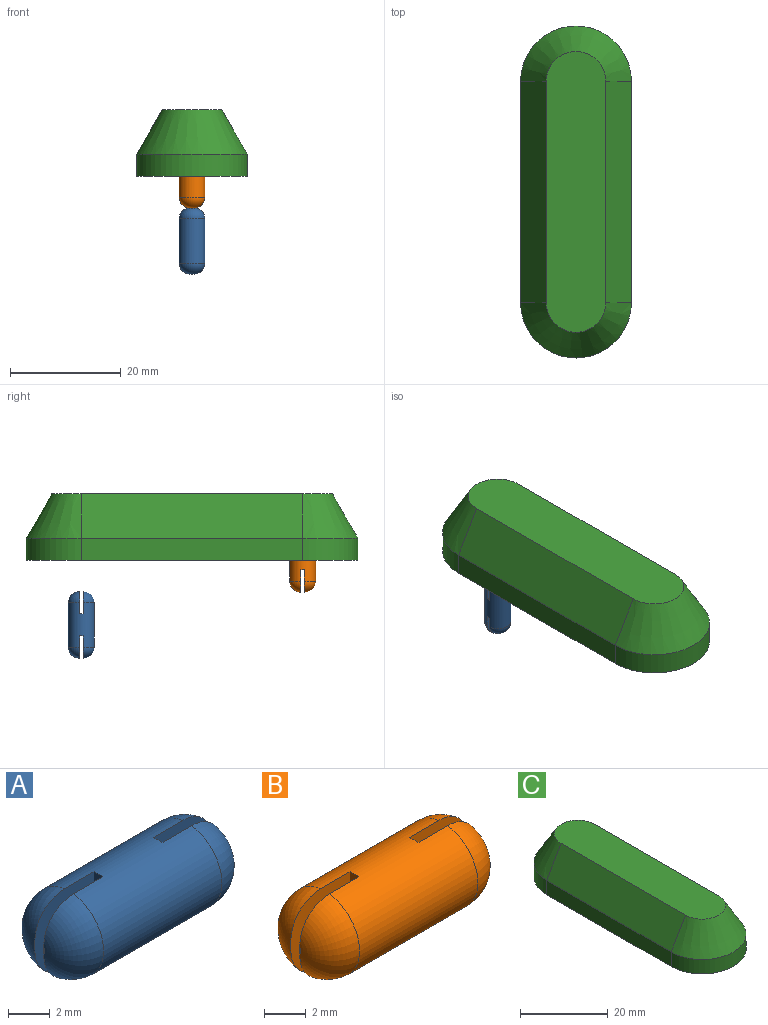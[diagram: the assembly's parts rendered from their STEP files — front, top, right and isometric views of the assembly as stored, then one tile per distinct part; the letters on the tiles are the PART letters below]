
ASSEMBLY  parts=3 mates=2
PART A: 15 faces, bbox 12x4.7x4.7 mm
  f0: plane 0.36x0.05mm, normal (1,0,0), area 0mm2, adj f1,f13
  f1: torus R=0.35mm, axis (1,0,0), area 14.1mm2, adj f0,f4,f13
  f2: plane 0.36x0.05mm, normal (-1,0,0), area 0mm2, adj f7,f10
  f3: torus R=0.35mm, axis (1,0,0), area 14.1mm2, adj f4,f6,f11
  f4: cylinder r=2.35mm len=8mm, axis (-1,0,0), area 113.3mm2, adj f1,f3,f7,f8,f9,f10,f11,f12
  f5: plane 0.36x0.05mm, normal (1,0,0), area 0mm2, adj f8,f14
  f6: plane 0.36x0.05mm, normal (-1,0,0), area 0mm2, adj f3,f11
  f7: torus R=0.35mm, axis (1,0,0), area 14.1mm2, adj f2,f4,f10
  f8: torus R=0.35mm, axis (1,0,0), area 14.1mm2, adj f4,f5,f14
  f9: plane 4.7x0.6mm, normal (-1,0,0), area 2.8mm2, adj f4,f10,f11
  f10: plane 4.66x4mm, normal (0,1,0), area 16.9mm2, adj f2,f4,f7,f9
  f11: plane 4.66x4mm, normal (0,-1,0), area 16.9mm2, adj f3,f4,f6,f9
  f12: plane 4.7x0.6mm, normal (1,0,0), area 2.8mm2, adj f4,f13,f14
  f13: plane 4.66x4mm, normal (0,1,0), area 16.9mm2, adj f0,f1,f4,f12
  f14: plane 4.66x4mm, normal (0,-1,0), area 16.9mm2, adj f4,f5,f8,f12
PART B: 15 faces, bbox 12x4.7x4.7 mm
  f0: plane 0.36x0.05mm, normal (1,0,0), area 0mm2, adj f1,f13
  f1: torus R=0.35mm, axis (1,0,0), area 14.1mm2, adj f0,f4,f13
  f2: plane 0.36x0.05mm, normal (-1,0,0), area 0mm2, adj f7,f10
  f3: torus R=0.35mm, axis (1,0,0), area 14.1mm2, adj f4,f6,f11
  f4: cylinder r=2.35mm len=8mm, axis (-1,0,0), area 113.3mm2, adj f1,f3,f7,f8,f9,f10,f11,f12
  f5: plane 0.36x0.05mm, normal (1,0,0), area 0mm2, adj f8,f14
  f6: plane 0.36x0.05mm, normal (-1,0,0), area 0mm2, adj f3,f11
  f7: torus R=0.35mm, axis (1,0,0), area 14.1mm2, adj f2,f4,f10
  f8: torus R=0.35mm, axis (1,0,0), area 14.1mm2, adj f4,f5,f14
  f9: plane 4.7x0.6mm, normal (-1,0,0), area 2.8mm2, adj f4,f10,f11
  f10: plane 4.66x4mm, normal (0,1,0), area 16.9mm2, adj f2,f4,f7,f9
  f11: plane 4.66x4mm, normal (0,-1,0), area 16.9mm2, adj f3,f4,f6,f9
  f12: plane 4.7x0.6mm, normal (1,0,0), area 2.8mm2, adj f4,f13,f14
  f13: plane 4.66x4mm, normal (0,1,0), area 16.9mm2, adj f0,f1,f4,f12
  f14: plane 4.66x4mm, normal (0,-1,0), area 16.9mm2, adj f4,f5,f8,f12
PART C: 16 faces, bbox 20x60x12 mm
  f0: plane 40x4mm, normal (-1,0,0), area 160mm2, adj f1,f3,f5,f6
  f1: cylinder r=10mm len=20mm, axis (0,0,-1), area 125.7mm2, adj f0,f2,f5,f7
  f2: plane 40x4mm, normal (1,0,0), area 160mm2, adj f1,f3,f5,f9
  f3: cylinder r=10mm len=20mm, axis (0,0,-1), area 125.7mm2, adj f0,f2,f5,f8
  f4: plane 50.76x10.76mm, normal (0,0,1), area 521.5mm2, adj f6,f7,f8,f9
  f5: plane 60x20mm, normal (0,0,-1), area 1074.9mm2, adj f0,f1,f2,f3,f10,f12
  f6: plane 40x8mm, normal (-0.87,0,0.5), area 369.5mm2, adj f0,f4,f7,f8
  f7: cone r=5.38mm half-angle=30deg, axis (0,0,-1), area 223.2mm2, adj f1,f4,f6,f9
  f8: cone r=5.38mm half-angle=30deg, axis (0,0,-1), area 223.2mm2, adj f3,f4,f6,f9
  f9: plane 40x8mm, normal (0.87,0,0.5), area 369.5mm2, adj f2,f4,f7,f8
  f10: cylinder r=2.5mm len=5mm, axis (0,0,-1), area 62.8mm2, adj f5,f15
  f11: plane 1x1mm, normal (0,0,-1), area 0.8mm2, adj f15
  f12: cylinder r=2.5mm len=5mm, axis (0,0,-1), area 62.8mm2, adj f5,f14
  f13: plane 1x1mm, normal (0,0,-1), area 0.8mm2, adj f14
  f14: cone r=2.5mm half-angle=45deg, axis (0,0,-1), area 26.7mm2, adj f12,f13
  f15: cone r=2.5mm half-angle=45deg, axis (0,0,-1), area 26.7mm2, adj f10,f11
PLACE A rot(axis=(0,-1,0),90deg) t=(7.12,16.92,-16.91)mm
PLACE B rot(axis=(0,-1,0),90deg) t=(-32.88,-23.08,-4.97)mm
PLACE C t=(-12.88,-3.08,0.78)mm fixed
MATE slider A.f1 <-> C.f10  axis (0,0,-1) through (-12.88,16.92,-10.91)mm
MATE slider B.f1 <-> C.f12  axis (0,0,-1) through (-12.88,-23.08,1.03)mm
